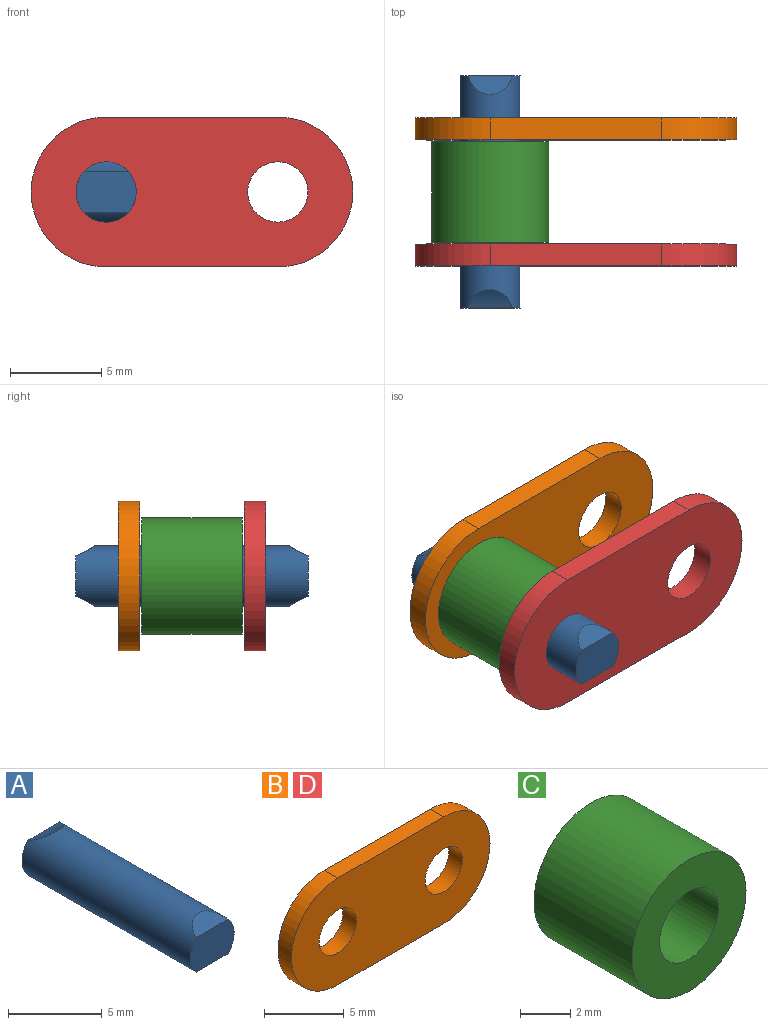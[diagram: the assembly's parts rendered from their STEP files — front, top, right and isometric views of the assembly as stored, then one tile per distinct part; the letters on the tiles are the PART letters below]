
ASSEMBLY  parts=4 mates=3
PART A: 7 faces, bbox 3.3x12.7x3.3 mm
  f0: plane 3.3x2.25mm, normal (0,-1,0), area 6.8mm2, adj f2,f3,f6
  f1: plane 3.3x2.25mm, normal (0,1,0), area 6.8mm2, adj f2,f4,f5
  f2: cylinder r=1.65mm len=12.7mm, axis (0,1,0), area 124mm2, adj f0,f1,f3,f4,f5,f6
  f3: cylinder r=3.3mm len=2.41mm, axis (1,0,0), area 2mm2, adj f0,f2
  f4: cylinder r=3.3mm len=2.41mm, axis (1,0,0), area 2mm2, adj f1,f2
  f5: cylinder r=3.3mm len=2.41mm, axis (1,0,0), area 2mm2, adj f1,f2
  f6: cylinder r=3.3mm len=2.41mm, axis (1,0,0), area 2mm2, adj f0,f2
PART B: 8 faces, bbox 17.6x1.2x8.2 mm
  f0: plane 9.4x1.2mm, normal (0,0,1), area 11.3mm2, adj f1,f5,f6,f7
  f1: cylinder r=4.1mm len=8.2mm, axis (0,1,0), area 15.5mm2, adj f0,f2,f6,f7
  f2: plane 9.4x1.2mm, normal (0,0,-1), area 11.3mm2, adj f1,f5,f6,f7
  f3: cylinder r=1.65mm len=3.3mm, axis (0,1,0), area 12.4mm2, adj f6,f7
  f4: cylinder r=1.65mm len=3.3mm, axis (0,1,0), area 12.4mm2, adj f6,f7
  f5: cylinder r=4.1mm len=8.2mm, axis (0,1,0), area 15.5mm2, adj f0,f2,f6,f7
  f6: plane 17.6x8.2mm, normal (0,-1,0), area 112.8mm2, adj f0,f1,f2,f3,f4,f5
  f7: plane 17.6x8.2mm, normal (0,1,0), area 112.8mm2, adj f0,f1,f2,f3,f4,f5
PART C: 4 faces, bbox 6.4x5.5x6.4 mm
  f0: cylinder r=1.65mm len=5.5mm, axis (0,1,0), area 57mm2, adj f2,f3
  f1: cylinder r=3.2mm len=6.4mm, axis (0,1,0), area 110.6mm2, adj f2,f3
  f2: plane 6.4x6.4mm, normal (0,-1,0), area 23.6mm2, adj f0,f1
  f3: plane 6.4x6.4mm, normal (0,1,0), area 23.6mm2, adj f0,f1
PART D: same geometry as B
PLACE A t=(0,-6.35,0)mm
PLACE B t=(0,4.05,0)mm
PLACE C t=(0,2.75,0)mm
PLACE D t=(0,-2.85,0)mm
MATE fastened D.f1 <-> C.f1  axis (0,1,0) through (0,-2.85,0)mm
MATE fastened B.f3 <-> C.f0  axis (0,1,0) through (0,2.85,0)mm
MATE fastened C.f1 <-> A.f2  axis (0,1,0) through (0,0,0)mm
